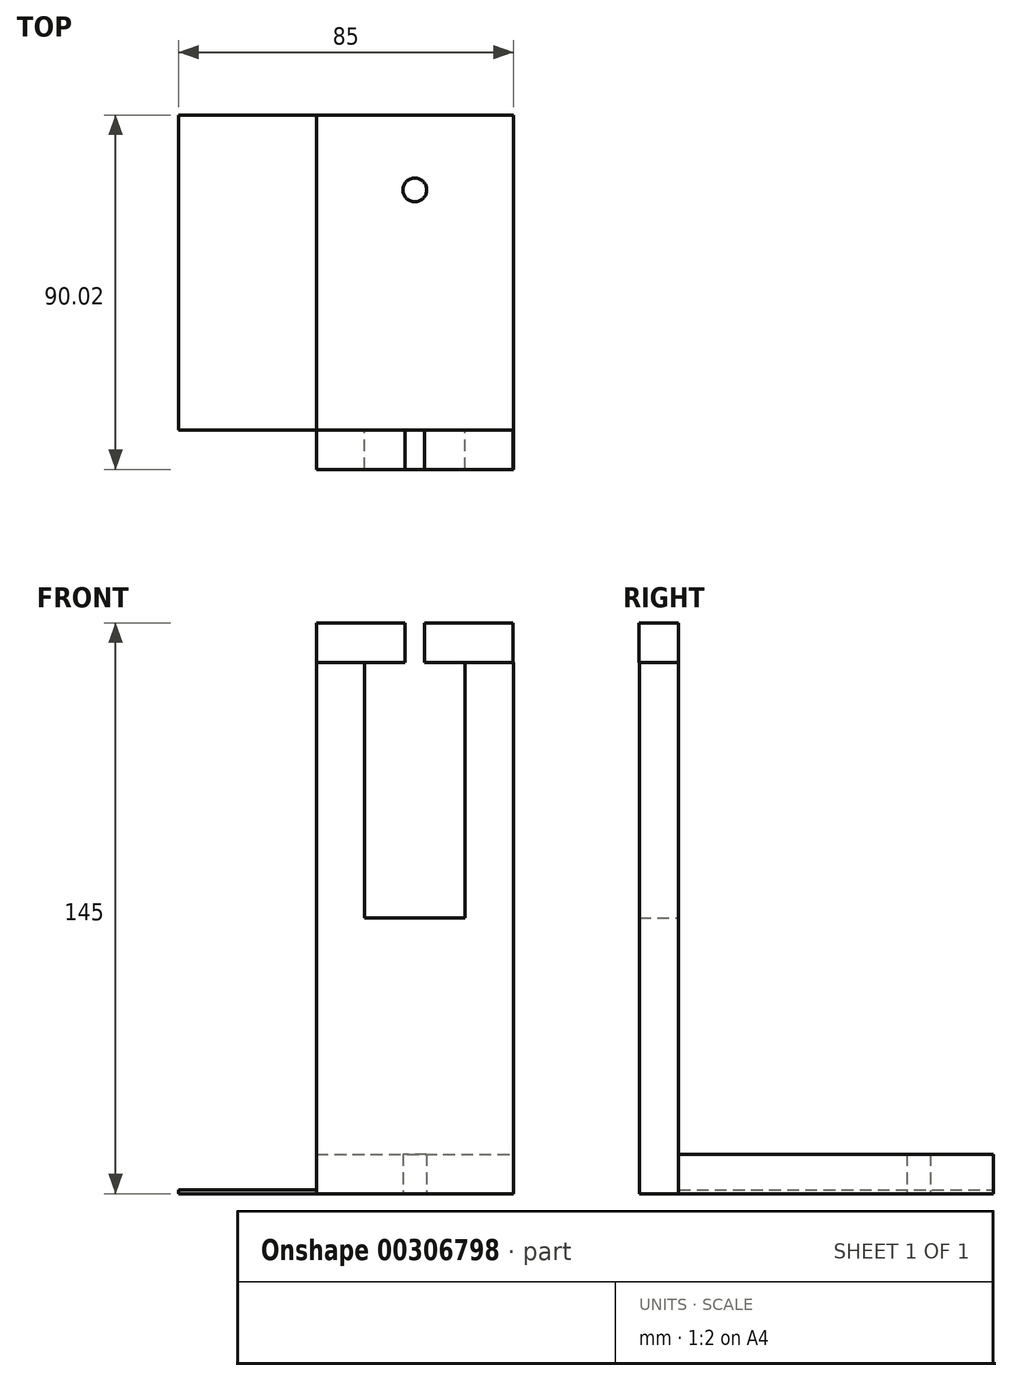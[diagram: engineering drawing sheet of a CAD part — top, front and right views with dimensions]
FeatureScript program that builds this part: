
annotation { "Feature Type Name" : "Feature", "Feature Type Description" : "" }
export const myFeature = defineFeature(function(context is Context, id is Id, definition is map)
    precondition{}
    {
        {
            var Q0;
            Q0=qCreatedBy(makeId("Top.planeOp"),FACE);
            var sketch = newSketch(context, id + "F0", { "sketchPlane" : qUnion([Q0])});
            skLineSegment(sketch, "E0", {"start": v(0, -40) * mm, "end": v(60, -40) * mm});
            skLineSegment(sketch, "E1", {"start": v(60, -40) * mm, "end": v(-60, -40) * mm});
            skLineSegment(sketch, "E2", {"start": v(-60, -40) * mm, "end": v(-60, 40) * mm});
            skLineSegment(sketch, "E3", {"start": v(-60, 40) * mm, "end": v(60, 40) * mm});
            skLineSegment(sketch, "E4", {"start": v(60, 40) * mm, "end": v(60, -40) * mm});
            skLineSegment(sketch, "E5", {"start": v(-60, -40) * mm, "end": v(-60, -50) * mm});
            skLineSegment(sketch, "E6", {"start": v(-60, -50) * mm, "end": v(60, -50) * mm});
            skLineSegment(sketch, "E7", {"start": v(60, -50) * mm, "end": v(60, -40) * mm});
            skLineSegment(sketch, "E8", {"start": v(0, -50) * mm, "end": v(-25, -50) * mm});
            skLineSegment(sketch, "E9", {"start": v(-25, -50) * mm, "end": v(25, -50) * mm});
            skLineSegment(sketch, "E10", {"start": v(25, -50) * mm, "end": v(25, -40) * mm});
            skLineSegment(sketch, "E11", {"start": v(-25, -50) * mm, "end": v(-25, -40) * mm});
            skLineSegment(sketch, "E12", {"start": v(-25, -50) * mm, "end": v(-12.75, -50) * mm});
            skLineSegment(sketch, "E13", {"start": v(-12.75, -50) * mm, "end": v(-12.75, -40) * mm});
            skLineSegment(sketch, "E14", {"start": v(25, -50) * mm, "end": v(12.75, -50) * mm});
            skLineSegment(sketch, "E15", {"start": v(12.75, -50) * mm, "end": v(12.75, -40) * mm});
            skLineSegment(sketch, "E16", {"start": v(0, 40) * mm, "end": v(0, 21) * mm, "construction": true});
            skPoint(sketch, "E16.endSnap0", {"position": v(0, 40) * mm});
            skCircle(sketch, "E17", {"center": v(0, 21) * mm, "radius": 3.02 * mm});
            skLineSegment(sketch, "E18", {"start": v(-25, -40) * mm, "end": v(-25, 40) * mm});
            skLineSegment(sketch, "E19", {"start": v(25, -40) * mm, "end": v(25, 40) * mm});
            skSolve(sketch);
        }
        {
            var Q0;
            {var subQ7=sQuery(id+"F0.wireOp",EDGE,"E2");Q0=makeQuery(id+"F0.imprint","IMPRINT",FACE,{"disambiguationData":[TD([[makeQuery(id+"F0.imprint","IMPRINT",EDGE,{"derivedFrom":subQ7}),-1.0]])]});}
            extrude(context, id + "F1", {"entities" : qUnion([Q0]), "depth" : 1 * mm});
        }
        {
            var Q0;
            {var subQ0=sQuery(id+"F0.wireOp",EDGE,"E11");Q0=makeQuery(id+"F0.imprint","IMPRINT",FACE,{"disambiguationData":[TD([[makeQuery(id+"F0.imprint","IMPRINT",EDGE,{"derivedFrom":subQ0}),-1.0]])]});}
            var Q1;
            {var subQ0=sQuery(id+"F0.wireOp",EDGE,"E10");Q1=makeQuery(id+"F0.imprint","IMPRINT",FACE,{"disambiguationData":[TD([[makeQuery(id+"F0.imprint","IMPRINT",EDGE,{"derivedFrom":subQ0}),1.0]])]});}
            extrude(context, id + "F2", {"entities" : qUnion([Q0, Q1]), "operationType" : NewBodyOperationType.ADD, "depth" : 135 * mm});
        }
        {
            var Q0;
            Q0=qCreatedBy(makeId("Top.planeOp"),FACE);
            cPlane(context, id + "F3", {"entities" : qUnion([Q0]), "cplaneType" : CPlaneType.OFFSET, "offset" : 135 * mm, "width" : 150 * mm, "height" : 150 * mm});
        }
        {
            var Q0;
            Q0=qCreatedBy(id+"F3.planeOp",FACE);
            var sketch = newSketch(context, id + "F4", { "sketchPlane" : qUnion([Q0])});
            skLineSegment(sketch, "E20.bottom", {"start": v(-25.03, -40.02) * mm, "end": v(24.97, -40.02) * mm});
            skLineSegment(sketch, "E20.top", {"start": v(-25.03, -50.02) * mm, "end": v(24.97, -50.02) * mm});
            skLineSegment(sketch, "E20.left", {"start": v(-25.03, -40.02) * mm, "end": v(-25.03, -50.02) * mm});
            skLineSegment(sketch, "E20.right", {"start": v(24.97, -40.02) * mm, "end": v(24.97, -50.02) * mm});
            skLineSegment(sketch, "E21", {"start": v(-25.03, -50.02) * mm, "end": v(-12.78, -50.02) * mm});
            skLineSegment(sketch, "E22", {"start": v(-25.03, -50.02) * mm, "end": v(-2.53, -50.02) * mm});
            skLineSegment(sketch, "E23", {"start": v(-2.53, -50.02) * mm, "end": v(-2.53, -40.02) * mm});
            skLineSegment(sketch, "E24", {"start": v(24.97, -50.02) * mm, "end": v(2.47, -50.02) * mm});
            skLineSegment(sketch, "E25", {"start": v(2.47, -50.02) * mm, "end": v(2.47, -40.02) * mm});
            skSolve(sketch);
        }
        {
            var Q0;
            {var subQ0=sQuery(id+"F4.wireOp",EDGE,"E20.left");Q0=makeQuery(id+"F4.imprint","IMPRINT",FACE,{"disambiguationData":[TD([[makeQuery(id+"F4.imprint","IMPRINT",EDGE,{"derivedFrom":subQ0}),1.0]])]});}
            var Q1;
            {var subQ0=sQuery(id+"F4.wireOp",EDGE,"E20.right");Q1=makeQuery(id+"F4.imprint","IMPRINT",FACE,{"disambiguationData":[TD([[makeQuery(id+"F4.imprint","IMPRINT",EDGE,{"derivedFrom":subQ0}),-1.0]])]});}
            extrude(context, id + "F5", {"entities" : qUnion([Q0, Q1]), "operationType" : NewBodyOperationType.ADD, "depth" : 10 * mm});
        }
        {
            var Q0;
            {var subQ0=sQuery(id+"F0.wireOp",EDGE,"E13");Q0=makeQuery(id+"F0.imprint","IMPRINT",FACE,{"disambiguationData":[TD([[makeQuery(id+"F0.imprint","IMPRINT",EDGE,{"derivedFrom":subQ0}),-1.0]])]});}
            extrude(context, id + "F6", {"entities" : qUnion([Q0]), "operationType" : NewBodyOperationType.ADD, "depth" : 70 * mm});
        }
        {
            var Q0;
            Q0=makeQuery(id+"F0.imprint","IMPRINT",FACE,{"disambiguationData":[TD([[makeQuery(id+"F0.imprint","IMPRINT",EDGE,{"derivedFrom":sQuery(id+"F0.wireOp",EDGE,"E17")}),-1.0]])]});
            extrude(context, id + "F7", {"entities" : qUnion([Q0]), "depth" : 10 * mm});
        }
    });
